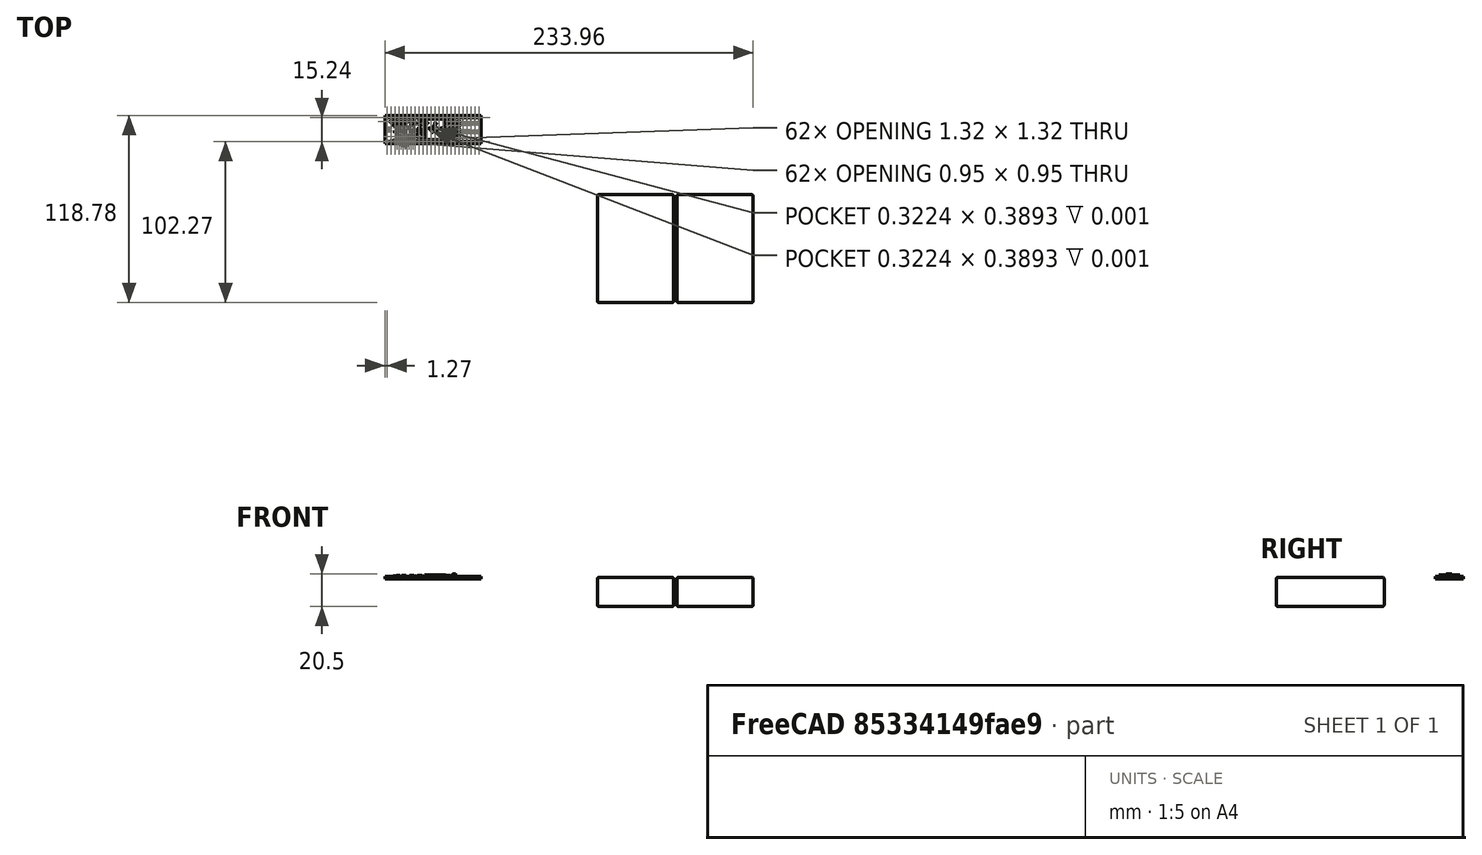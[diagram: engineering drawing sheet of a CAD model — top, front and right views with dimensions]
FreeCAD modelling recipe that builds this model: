
FCSTD DOCUMENT  (FreeCAD 0.18R4 (GitTag))
Label: Datalogger with Teensy
License: All rights reserved
LicenseURL: http://en.wikipedia.org/wiki/All_rights_reserved
objects: Part::Feature×3, App::VRMLObject×2, Part::Box×2, Part::Fillet×2, App::Part×1
note: 7 computed .brp shape members not serialized (recipe doc carries the construction recipe); baked Part::Feature solids carry a one-line shape summary decoded from their .brp

FEATURE [App::VRMLObject] Light_intensity_data_logger
  Resources = Light_intensity_data_logger/shapes3D/C_0603.wrl | Light_intensity_data_logger/shapes3D/Display with header.wrl | Light_intensity_data_logger/shapes3D/Teensy 35_36 - doublewide header only.wrl | Light_intensity_data_logger/shapes3D/BU2032SM-BT-GTR.wrl | Light_intensity_data_logger/shapes3D/Banana connector.wrl | Light_intensity_data_logger/shapes3D/D_SOD-323.wrl | Light_intensity_data_logger/shapes3D/TCS37727FN.wrl | Light_intensity_data_logger/shapes3D/C_1206.wrl | Light_intensity_data_logger/shapes3D/BME280.wrl | Light_intensity_data_logger/shapes3D/TSL25911FN.wrl | Light_intensity_data_logger/shapes3D/JS202011SCQN.wrl | Light_intensity_data_logger/shapes3D/JS5208.wrl | Light_intensity_data_logger/shapes3D/1506 8x resistor array.wrl | Light_intensity_data_logger/shapes3D/R_0603.wrl | Light_intensity_data_logger/shapes3D/SOT-363_SC-70-6.wrl
FEATURE [Part::Feature] Part__Feature  label="Teensy 3_5"
  shape: bbox 60.96 x 17.78 x 3.062 mm, 1427 faces, 74 solids (baked)
FEATURE [Part::Feature] Part__Feature001  label="DM3D-SF"
  Placement = pos=(-9.15759,6.51929,0) rot=(0,0,1;1.5708rad)
  shape: bbox 11.46 x 11.96 x 1.563 mm, 957 faces, 0 solids (baked)
FEATURE [Part::Feature] Part__Feature002  label="473460001"
  Placement = pos=(-58.5674,8.82223,1.23741) rot=(0.57735,-0.57735,-0.57735;2.0944rad)
  shape: bbox 5.43 x 7.98 x 2.94 mm, 408 faces, 0 solids (baked)
FEATURE [App::Part] Teensy_3_6  label="Teensy 3_6"
  Group = -> [Part__Feature,Part__Feature001,Part__Feature002]
  Origin = -> Origin
  Placement = pos=(82.5,-74.6,9.7) rot=(0,0,1;3.14159rad)
FEATURE [Part::Box] Box  label="Cube"
  AttacherType = Attacher::AttachEngine3D
  Height = 18.5
  Length = 48.5
  Width = 68.5
FEATURE [Part::Fillet] Fillet  label="Battery Pack 1"
  Base = -> Box
  Edges = 12 edges r=1: [Edge1,Edge2,Edge3,Edge4,Edge5,Edge6,Edge7,Edge8,Edge9,Edge10,Edge11,Edge12]
  Placement = pos=(124.5,-101,-19) rot=(0,0,1;0rad)
FEATURE [Part::Box] Box001  label="Cube001"
  AttacherType = Attacher::AttachEngine3D
  Height = 18.5
  Length = 48.5
  Width = 68.5
FEATURE [Part::Fillet] Fillet001  label="Battery Pack 2"
  Base = -> Box001
  Edges = 12 edges r=1: [Edge1,Edge2,Edge3,Edge4,Edge5,Edge6,Edge7,Edge8,Edge9,Edge10,Edge11,Edge12]
  Placement = pos=(74,-101,-19) rot=(0,0,1;0rad)
FEATURE [App::VRMLObject] Light_intensity_data_logger_PCBWay  label="Light_intensity_data_logger-PCBWay"
  Resources = Light_intensity_data_logger_PCBWay/shapes3D/Display with header.wrl | Light_intensity_data_logger_PCBWay/shapes3D/JS5208.wrl | Light_intensity_data_logger_PCBWay/shapes3D/C_0603.wrl | Light_intensity_data_logger_PCBWay/shapes3D/Teensy 35_36 - doublewide header only.wrl | Light_intensity_data_logger_PCBWay/shapes3D/BU2032SM-BT-GTR.wrl | Light_intensity_data_logger_PCBWay/shapes3D/Banana connector.wrl | Light_intensity_data_logger_PCBWay/shapes3D/D_SOD-323.wrl | Light_intensity_data_logger_PCBWay/shapes3D/TCS37727FN.wrl | Light_intensity_data_logger_PCBWay/shapes3D/C_1206.wrl | Light_intensity_data_logger_PCBWay/shapes3D/BME280.wrl | Light_intensity_data_logger_PCBWay/shapes3D/TSL25911FN.wrl | Light_intensity_data_logger_PCBWay/shapes3D/JS202011SCQN.wrl | Light_intensity_data_logger_PCBWay/shapes3D/1506 8x resistor array.wrl | Light_intensity_data_logger_PCBWay/shapes3D/R_0603.wrl | Light_intensity_data_logger_PCBWay/shapes3D/SOT-363_SC-70-6.wrl
